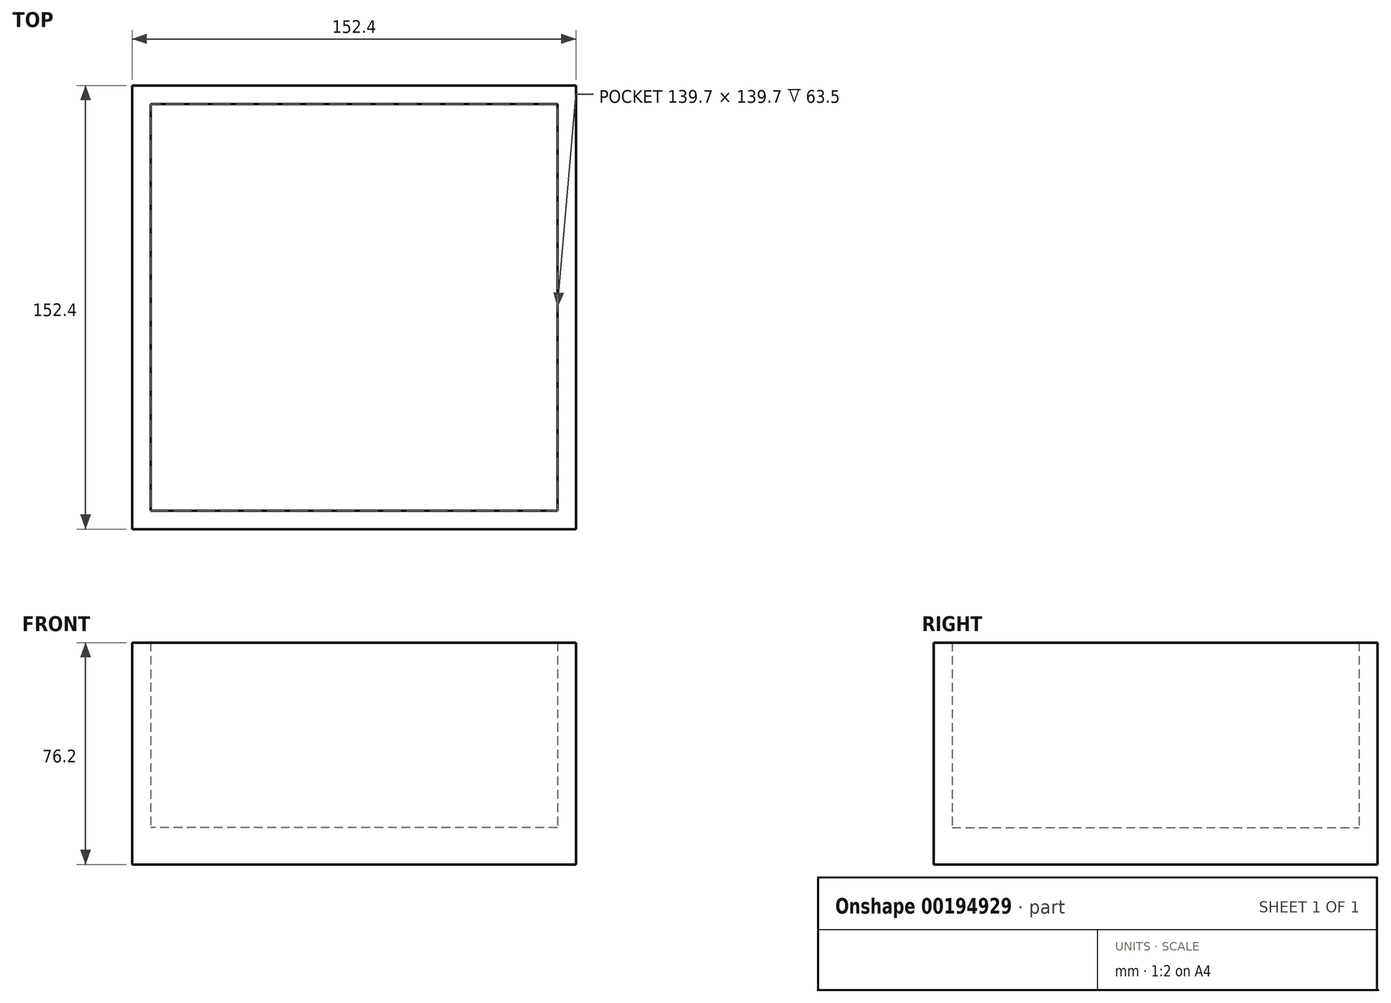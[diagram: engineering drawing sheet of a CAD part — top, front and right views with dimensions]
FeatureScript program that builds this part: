
annotation { "Feature Type Name" : "Feature", "Feature Type Description" : "" }
export const myFeature = defineFeature(function(context is Context, id is Id, definition is map)
    precondition{}
    {
        {
            var Q0;
            Q0=qCreatedBy(makeId("Top.planeOp"),FACE);
            var sketch = newSketch(context, id + "F0", { "sketchPlane" : qUnion([Q0])});
            skLineSegment(sketch, "E0.bottom", {"start": v(76.2, -76.2) * mm, "end": v(-76.2, -76.2) * mm});
            skLineSegment(sketch, "E0.top", {"start": v(76.2, 76.2) * mm, "end": v(-76.2, 76.2) * mm});
            skLineSegment(sketch, "E0.left", {"start": v(76.2, -76.2) * mm, "end": v(76.2, 76.2) * mm});
            skLineSegment(sketch, "E0.right", {"start": v(-76.2, -76.2) * mm, "end": v(-76.2, 76.2) * mm});
            skPoint(sketch, "E0.middle", {"position": v(0, 0) * mm});
            skLineSegment(sketch, "E1.bottom", {"start": v(69.85, -69.85) * mm, "end": v(-69.85, -69.85) * mm});
            skLineSegment(sketch, "E1.top", {"start": v(69.85, 69.85) * mm, "end": v(-69.85, 69.85) * mm});
            skLineSegment(sketch, "E1.left", {"start": v(69.85, -69.85) * mm, "end": v(69.85, 69.85) * mm});
            skLineSegment(sketch, "E1.right", {"start": v(-69.85, -69.85) * mm, "end": v(-69.85, 69.85) * mm});
            skSolve(sketch);
        }
        {
            var Q0;
            Q0=makeQuery(id+"F0.imprint","IMPRINT",FACE,{"disambiguationData":[TD([[makeQuery(id+"F0.imprint","IMPRINT",EDGE,{"derivedFrom":sQuery(id+"F0.wireOp",EDGE,"E0.bottom")}),-1.0]])]});
            extrude(context, id + "F1", {"entities" : qUnion([Q0]), "depth" : 76.2 * mm});
        }
        {
            var Q0;
            Q0=qCreatedBy(makeId("Top.planeOp"),FACE);
            var sketch = newSketch(context, id + "F2", { "sketchPlane" : qUnion([Q0])});
            skLineSegment(sketch, "E2.bottom", {"start": v(69.85, -69.85) * mm, "end": v(-69.85, -69.85) * mm});
            skLineSegment(sketch, "E2.top", {"start": v(69.85, 69.85) * mm, "end": v(-69.85, 69.85) * mm});
            skLineSegment(sketch, "E2.left", {"start": v(69.85, -69.85) * mm, "end": v(69.85, 69.85) * mm});
            skLineSegment(sketch, "E2.right", {"start": v(-69.85, -69.85) * mm, "end": v(-69.85, 69.85) * mm});
            skPoint(sketch, "E2.middle", {"position": v(0, 0) * mm});
            skSolve(sketch);
        }
        {
            var Q0;
            Q0=makeQuery(id+"F2.imprint","IMPRINT",FACE,{"disambiguationData":[TD([[makeQuery(id+"F2.imprint","IMPRINT",EDGE,{"derivedFrom":sQuery(id+"F2.wireOp",EDGE,"E2.bottom")}),-1.0]])]});
            extrude(context, id + "F3", {"entities" : qUnion([Q0]), "operationType" : NewBodyOperationType.ADD, "depth" : 12.7 * mm});
        }
    });
